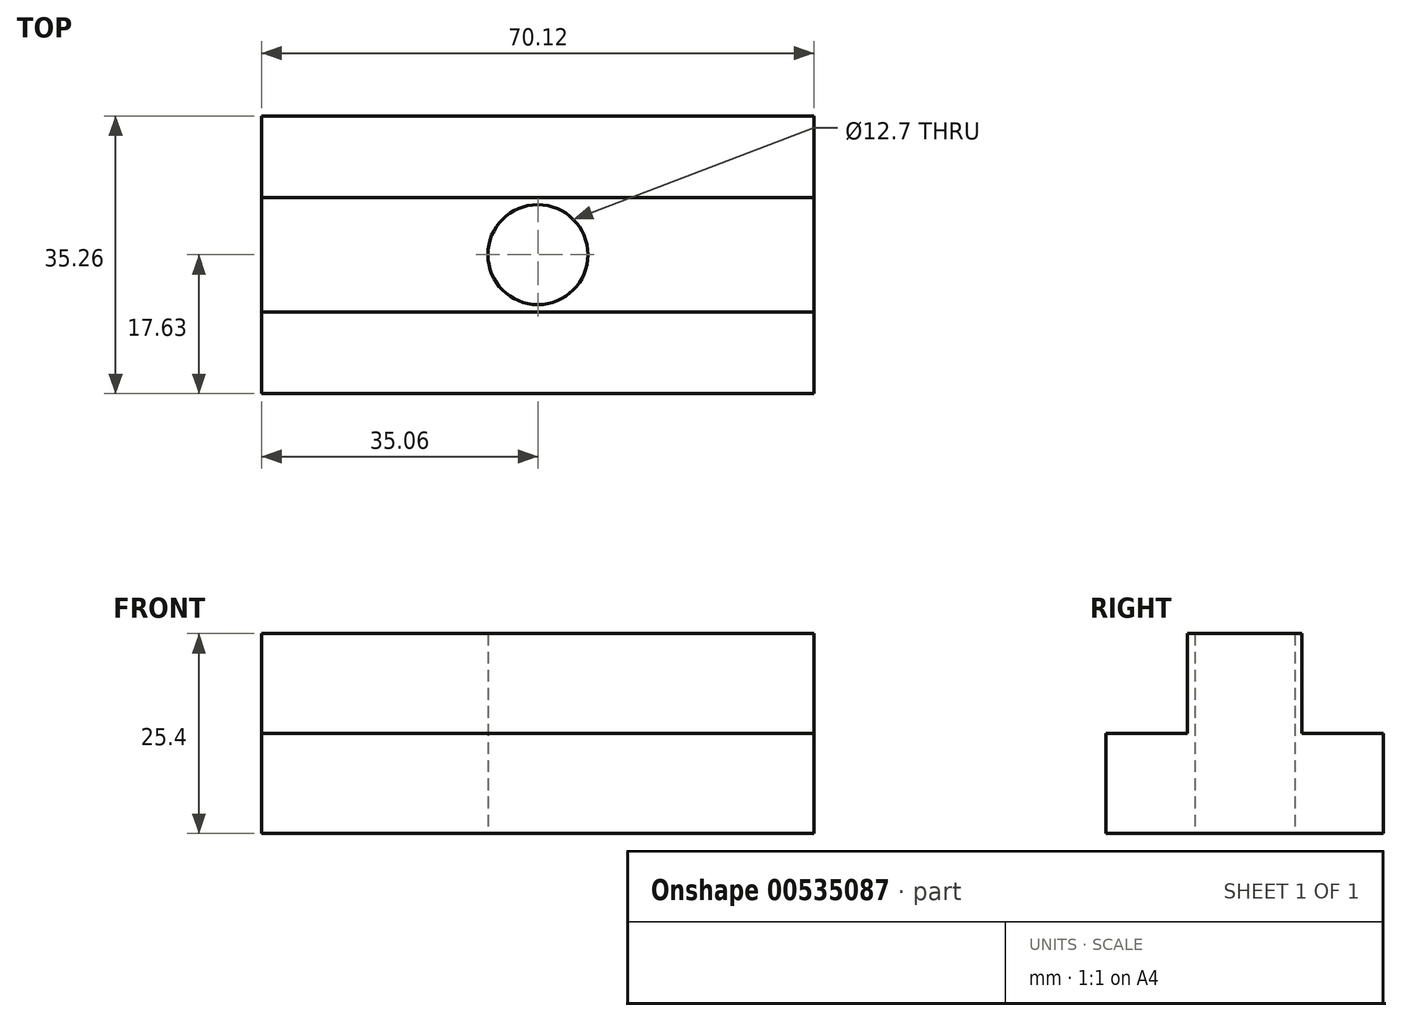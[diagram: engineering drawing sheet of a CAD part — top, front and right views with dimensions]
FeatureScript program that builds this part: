
annotation { "Feature Type Name" : "Feature", "Feature Type Description" : "" }
export const myFeature = defineFeature(function(context is Context, id is Id, definition is map)
    precondition{}
    {
        {
            var Q0;
            Q0=qCreatedBy(makeId("Top.planeOp"),FACE);
            var sketch = newSketch(context, id + "F0", { "sketchPlane" : qUnion([Q0])});
            skLineSegment(sketch, "E0.bottom", {"start": v(35.06, -17.63) * mm, "end": v(-35.06, -17.63) * mm});
            skLineSegment(sketch, "E0.top", {"start": v(35.06, 17.63) * mm, "end": v(-35.06, 17.63) * mm});
            skLineSegment(sketch, "E0.left", {"start": v(35.06, -17.63) * mm, "end": v(35.06, 17.63) * mm});
            skLineSegment(sketch, "E0.right", {"start": v(-35.06, -17.63) * mm, "end": v(-35.06, 17.63) * mm});
            skPoint(sketch, "E0.middle", {"position": v(0, 0) * mm});
            skLineSegment(sketch, "E1.bottom", {"start": v(35.06, -7.26) * mm, "end": v(-35.06, -7.26) * mm});
            skLineSegment(sketch, "E1.top", {"start": v(35.06, 7.26) * mm, "end": v(-35.06, 7.26) * mm});
            skLineSegment(sketch, "E1.left", {"start": v(35.06, -7.26) * mm, "end": v(35.06, 7.26) * mm});
            skLineSegment(sketch, "E1.right", {"start": v(-35.06, -7.26) * mm, "end": v(-35.06, 7.26) * mm});
            skSolve(sketch);
        }
        {
            var Q0;
            Q0 = qSketchRegion(id + "F0", true);
            extrude(context, id + "F1", {"entities" : qUnion([Q0]), "oppositeDirection" : true, "depth" : 12.7 * mm, "offsetDistance" : 25.4 * mm});
        }
        {
            var Q0;
            Q0=makeQuery(id+"F0.imprint","IMPRINT",FACE,{"disambiguationData":[TD([[makeQuery(id+"F0.imprint","IMPRINT",EDGE,{"derivedFrom":sQuery(id+"F0.wireOp",EDGE,"E1.bottom")}),-1.0]])]});
            extrude(context, id + "F2", {"entities" : qUnion([Q0]), "operationType" : NewBodyOperationType.ADD, "depth" : 12.7 * mm, "offsetDistance" : 25.4 * mm});
        }
        {
            var Q0;
            Q0=makeQuery(id+"F2.opExtrude","CAP_FACE",FACE,{"disambiguationData":[OSD([sQuery(id+"F0.wireOp",EDGE,"E1.bottom"),sQuery(id+"F0.wireOp",EDGE,"E1.top"),sQuery(id+"F0.wireOp",EDGE,"E1.left"),sQuery(id+"F0.wireOp",EDGE,"E1.right")])],"isStart":false});
            var sketch = newSketch(context, id + "F3", { "sketchPlane" : qUnion([Q0])});
            skCircle(sketch, "E2", {"center": v(0, 0) * mm, "radius": 6.7 * mm});
            skSolve(sketch);
        }
        {
            var Q0;
            Q0=sQuery(id+"F3.wireOp",VERTEX,"E2.center");
            var Q1;
            Q1=makeQuery(id+"F1.opExtrude","SWEPT_BODY",BODY,{"disambiguationData":[OSD([sQuery(id+"F0.wireOp",EDGE,"E0.bottom"),sQuery(id+"F0.wireOp",EDGE,"E0.top"),sQuery(id+"F0.wireOp",EDGE,"E0.left"),sQuery(id+"F0.wireOp",EDGE,"E0.right"),sQuery(id+"F0.wireOp",EDGE,"E1.left"),sQuery(id+"F0.wireOp",EDGE,"E1.right")])]});
            hole(context, id + "F4", {"style" : HoleStyle.SIMPLE, "endStyle" : HoleEndStyle.THROUGH, "holeDiameter" : 12.7 * mm, "isTappedThrough" : true, "tappedDepth" : 12.7 * mm, "tapClearance" : 3, "locations" : qUnion([Q0]), "scope" : qUnion([Q1])});
        }
    });
